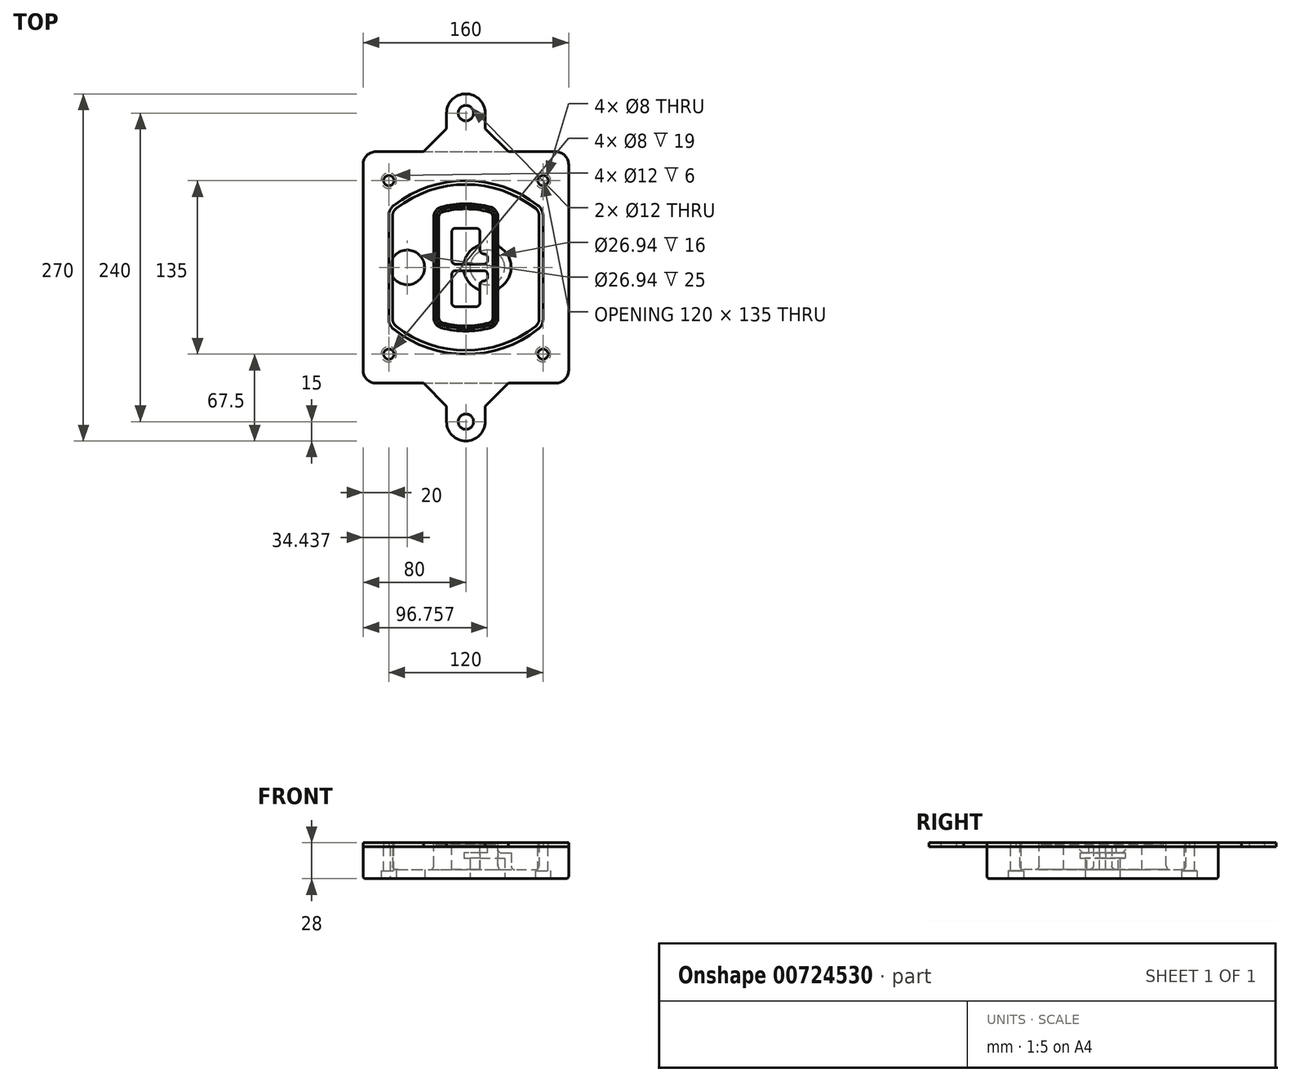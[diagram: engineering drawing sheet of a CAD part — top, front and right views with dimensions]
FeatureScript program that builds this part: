
annotation { "Feature Type Name" : "Feature", "Feature Type Description" : "" }
export const myFeature = defineFeature(function(context is Context, id is Id, definition is map)
    precondition{}
    {
        {
            var Q0;
            Q0=qCreatedBy(makeId("Top.planeOp"),FACE);
            var sketch = newSketch(context, id + "F0", { "sketchPlane" : qUnion([Q0])});
            skPoint(sketch, "E0.rect.middle", {"position": v(0, 0) * mm});
            skLineSegment(sketch, "E1.bottom", {"start": v(-70, -90) * mm, "end": v(70, -90) * mm});
            skLineSegment(sketch, "E1.top", {"start": v(-70, 90) * mm, "end": v(70, 90) * mm});
            skLineSegment(sketch, "E1.left", {"start": v(-80, -80) * mm, "end": v(-80, 80) * mm});
            skLineSegment(sketch, "E1.right", {"start": v(80, -80) * mm, "end": v(80, 80) * mm});
            skLineSegment(sketch, "E2", {"start": v(-80, 90) * mm, "end": v(80, -90) * mm, "construction": true});
            skLineSegment(sketch, "E3", {"start": v(80, 90) * mm, "end": v(-80, -90) * mm, "construction": true});
            skCircle(sketch, "E4", {"center": v(-60, 67.5) * mm, "radius": 4 * mm});
            skCircle(sketch, "E5", {"center": v(60, 67.5) * mm, "radius": 4 * mm});
            skCircle(sketch, "E6", {"center": v(60, -67.5) * mm, "radius": 4 * mm});
            skCircle(sketch, "E7", {"center": v(-60, -67.5) * mm, "radius": 4 * mm});
            skLineSegment(sketch, "E8", {"start": v(-60, 67.5) * mm, "end": v(60, 67.5) * mm, "construction": true});
            skLineSegment(sketch, "E9", {"start": v(60, 67.5) * mm, "end": v(60, -67.5) * mm, "construction": true});
            skLineSegment(sketch, "E10", {"start": v(60, -67.5) * mm, "end": v(-60, -67.5) * mm, "construction": true});
            skLineSegment(sketch, "E11", {"start": v(-60, -67.5) * mm, "end": v(-60, 67.5) * mm, "construction": true});
            skLineSegment(sketch, "E12", {"start": v(-60, 40.3) * mm, "end": v(-60, -40.3) * mm});
            skLineSegment(sketch, "E13", {"start": v(60, 40.3) * mm, "end": v(60, -40.3) * mm});
            skArc(sketch, "E14", {"start": v(56.15, 48.18) * mm, "mid": v(0, 67.5) * mm, "end": v(-56.15, 48.18) * mm});
            skArc(sketch, "E15", {"start": v(-56.15, -48.18) * mm, "mid": v(0, -67.5) * mm, "end": v(56.15, -48.18) * mm});
            skLineSegment(sketch, "E16", {"start": v(-60, 0) * mm, "end": v(60, 0) * mm, "construction": true});
            skPoint(sketch, "E17.visualSharp", {"position": v(-60, -45) * mm});
            skArc(sketch, "E17.filletArc", {"start": v(-60, -40.3) * mm, "mid": v(-58.99, -44.68) * mm, "end": v(-56.15, -48.18) * mm});
            skPoint(sketch, "E18.visualSharp", {"position": v(-60, 45) * mm});
            skArc(sketch, "E18.filletArc", {"start": v(-56.15, 48.18) * mm, "mid": v(-58.99, 44.68) * mm, "end": v(-60, 40.3) * mm});
            skPoint(sketch, "E19.visualSharp", {"position": v(60, 45) * mm});
            skArc(sketch, "E19.filletArc", {"start": v(60, 40.3) * mm, "mid": v(58.99, 44.68) * mm, "end": v(56.15, 48.18) * mm});
            skPoint(sketch, "E20.visualSharp", {"position": v(60, -45) * mm});
            skArc(sketch, "E20.filletArc", {"start": v(56.15, -48.18) * mm, "mid": v(58.99, -44.68) * mm, "end": v(60, -40.3) * mm});
            skPoint(sketch, "E21.visualSharp", {"position": v(-80, 90) * mm});
            skArc(sketch, "E21.filletArc", {"start": v(-70, 90) * mm, "mid": v(-77.07, 87.07) * mm, "end": v(-80, 80) * mm});
            skPoint(sketch, "E22.visualSharp", {"position": v(80, 90) * mm});
            skArc(sketch, "E22.filletArc", {"start": v(80, 80) * mm, "mid": v(77.07, 87.07) * mm, "end": v(70, 90) * mm});
            skPoint(sketch, "E23.visualSharp", {"position": v(80, -90) * mm});
            skArc(sketch, "E23.filletArc", {"start": v(70, -90) * mm, "mid": v(77.07, -87.07) * mm, "end": v(80, -80) * mm});
            skPoint(sketch, "E24.visualSharp", {"position": v(-80, -90) * mm});
            skArc(sketch, "E24.filletArc", {"start": v(-80, -80) * mm, "mid": v(-77.07, -87.07) * mm, "end": v(-70, -90) * mm});
            skArc(sketch, "E25.0", {"start": v(57, 40.3) * mm, "mid": v(56.3, 43.36) * mm, "end": v(54.3, 45.81) * mm});
            skLineSegment(sketch, "E25.1", {"start": v(57, 40.3) * mm, "end": v(57, -40.3) * mm});
            skArc(sketch, "E25.2", {"start": v(54.3, -45.81) * mm, "mid": v(56.3, -43.36) * mm, "end": v(57, -40.3) * mm});
            skArc(sketch, "E25.3", {"start": v(-54.3, -45.81) * mm, "mid": v(0, -64.5) * mm, "end": v(54.3, -45.81) * mm});
            skArc(sketch, "E25.4", {"start": v(-57, -40.3) * mm, "mid": v(-56.3, -43.36) * mm, "end": v(-54.3, -45.81) * mm});
            skArc(sketch, "E25.5", {"start": v(54.3, 45.81) * mm, "mid": v(0, 64.5) * mm, "end": v(-54.3, 45.81) * mm});
            skLineSegment(sketch, "E25.6", {"start": v(-57, 40.3) * mm, "end": v(-57, -40.3) * mm});
            skArc(sketch, "E25.7", {"start": v(-54.3, 45.81) * mm, "mid": v(-56.3, 43.36) * mm, "end": v(-57, 40.3) * mm});
            skArc(sketch, "E26.0", {"start": v(-58.62, 51.33) * mm, "mid": v(-62.58, 46.43) * mm, "end": v(-64, 40.3) * mm});
            skArc(sketch, "E26.1", {"start": v(58.62, 51.33) * mm, "mid": v(0, 71.5) * mm, "end": v(-58.62, 51.33) * mm});
            skArc(sketch, "E26.2", {"start": v(64, 40.3) * mm, "mid": v(62.58, 46.43) * mm, "end": v(58.62, 51.33) * mm});
            skLineSegment(sketch, "E26.3", {"start": v(64, 40.3) * mm, "end": v(64, -40.3) * mm});
            skArc(sketch, "E26.4", {"start": v(58.62, -51.33) * mm, "mid": v(62.58, -46.43) * mm, "end": v(64, -40.3) * mm});
            skLineSegment(sketch, "E26.5", {"start": v(-64, 40.3) * mm, "end": v(-64, -40.3) * mm});
            skArc(sketch, "E26.6", {"start": v(-58.62, -51.33) * mm, "mid": v(0, -71.5) * mm, "end": v(58.62, -51.33) * mm});
            skArc(sketch, "E26.7", {"start": v(-64, -40.3) * mm, "mid": v(-62.58, -46.43) * mm, "end": v(-58.62, -51.33) * mm});
            skSolve(sketch);
        }
        {
            var Q0;
            Q0=makeQuery(id+"F0.imprint","IMPRINT",FACE,{"disambiguationData":[TD([[makeQuery(id+"F0.imprint","IMPRINT",EDGE,{"derivedFrom":sQuery(id+"F0.wireOp",EDGE,"E1.bottom")}),1.0]])]});
            var Q1;
            Q1=makeQuery(id+"F0.imprint","IMPRINT",FACE,{"disambiguationData":[TD([[makeQuery(id+"F0.imprint","IMPRINT",EDGE,{"derivedFrom":sQuery(id+"F0.wireOp",EDGE,"E12")}),1.0]])]});
            var Q2;
            Q2=makeQuery(id+"F0.imprint","IMPRINT",FACE,{"disambiguationData":[TD([[makeQuery(id+"F0.imprint","IMPRINT",EDGE,{"derivedFrom":sQuery(id+"F0.wireOp",EDGE,"E25.0")}),1.0]])]});
            var Q3;
            Q3=makeQuery(id+"F0.imprint","IMPRINT",FACE,{"disambiguationData":[TD([[makeQuery(id+"F0.imprint","IMPRINT",EDGE,{"derivedFrom":sQuery(id+"F0.wireOp",EDGE,"E12")}),-1.0]])]});
            extrude(context, id + "F1", {"entities" : qUnion([Q0, Q1, Q2, Q3]), "oppositeDirection" : true, "depth" : 25 * mm});
        }
        {
            var Q0;
            Q0=makeQuery(id+"F0.imprint","IMPRINT",FACE,{"disambiguationData":[TD([[makeQuery(id+"F0.imprint","IMPRINT",EDGE,{"derivedFrom":sQuery(id+"F0.wireOp",EDGE,"E12")}),1.0]])]});
            extrude(context, id + "F2", {"entities" : qUnion([Q0]), "operationType" : NewBodyOperationType.ADD, "depth" : 3 * mm});
        }
        {
            var Q0;
            Q0=makeQuery(id+"F0.imprint","IMPRINT",FACE,{"disambiguationData":[TD([[makeQuery(id+"F0.imprint","IMPRINT",EDGE,{"derivedFrom":sQuery(id+"F0.wireOp",EDGE,"E25.0")}),1.0]])]});
            extrude(context, id + "F3", {"entities" : qUnion([Q0]), "operationType" : NewBodyOperationType.REMOVE, "oppositeDirection" : true, "depth" : 18 * mm});
        }
        {
            var Q0;
            Q0=makeQuery(id+"F2.opExtrude","CAP_FACE",FACE,{"disambiguationData":[OSD([sQuery(id+"F0.wireOp",EDGE,"E12"),sQuery(id+"F0.wireOp",EDGE,"E13"),sQuery(id+"F0.wireOp",EDGE,"E14"),sQuery(id+"F0.wireOp",EDGE,"E15"),sQuery(id+"F0.wireOp",EDGE,"E17.filletArc"),sQuery(id+"F0.wireOp",EDGE,"E18.filletArc"),sQuery(id+"F0.wireOp",EDGE,"E19.filletArc"),sQuery(id+"F0.wireOp",EDGE,"E20.filletArc"),sQuery(id+"F0.wireOp",EDGE,"E25.0"),sQuery(id+"F0.wireOp",EDGE,"E25.1"),sQuery(id+"F0.wireOp",EDGE,"E25.2"),sQuery(id+"F0.wireOp",EDGE,"E25.3"),sQuery(id+"F0.wireOp",EDGE,"E25.4"),sQuery(id+"F0.wireOp",EDGE,"E25.5"),sQuery(id+"F0.wireOp",EDGE,"E25.6"),sQuery(id+"F0.wireOp",EDGE,"E25.7")])],"isStart":false});
            var sketch = newSketch(context, id + "F4", { "sketchPlane" : qUnion([Q0])});
            skArc(sketch, "E27.0", {"start": v(-19.08, -46.97) * mm, "mid": v(0, -49.5) * mm, "end": v(19.08, -46.97) * mm});
            skArc(sketch, "E28.0", {"start": v(19.08, 46.97) * mm, "mid": v(0, 49.5) * mm, "end": v(-19.08, 46.97) * mm});
            skLineSegment(sketch, "E29", {"start": v(-25, 39.25) * mm, "end": v(-25, -39.25) * mm});
            skLineSegment(sketch, "E30", {"start": v(25, 39.25) * mm, "end": v(25, -39.25) * mm});
            skLineSegment(sketch, "E31", {"start": v(-25, 45.1) * mm, "end": v(25, 45.1) * mm, "construction": true});
            skLineSegment(sketch, "E32", {"start": v(-25, -45.1) * mm, "end": v(25, -45.1) * mm, "construction": true});
            skPoint(sketch, "E33.visualSharp", {"position": v(-25, 45.1) * mm});
            skArc(sketch, "E33.filletArc", {"start": v(-19.08, 46.97) * mm, "mid": v(-23.35, 44.11) * mm, "end": v(-25, 39.25) * mm});
            skPoint(sketch, "E34.visualSharp", {"position": v(25, 45.1) * mm});
            skArc(sketch, "E34.filletArc", {"start": v(25, 39.25) * mm, "mid": v(23.35, 44.11) * mm, "end": v(19.08, 46.97) * mm});
            skPoint(sketch, "E35.visualSharp", {"position": v(25, -45.1) * mm});
            skArc(sketch, "E35.filletArc", {"start": v(19.08, -46.97) * mm, "mid": v(23.35, -44.11) * mm, "end": v(25, -39.25) * mm});
            skPoint(sketch, "E36.visualSharp", {"position": v(-25, -45.1) * mm});
            skArc(sketch, "E36.filletArc", {"start": v(-25, -39.25) * mm, "mid": v(-23.35, -44.11) * mm, "end": v(-19.08, -46.97) * mm});
            skArc(sketch, "E37.0", {"start": v(54.3, 45.81) * mm, "mid": v(0, 64.5) * mm, "end": v(-54.3, 45.81) * mm});
            skArc(sketch, "E37.1", {"start": v(-54.3, 45.81) * mm, "mid": v(-56.3, 43.36) * mm, "end": v(-57, 40.3) * mm});
            skLineSegment(sketch, "E37.2", {"start": v(-57, 40.3) * mm, "end": v(-57, -40.3) * mm});
            skArc(sketch, "E37.3", {"start": v(-57, -40.3) * mm, "mid": v(-56.3, -43.36) * mm, "end": v(-54.3, -45.81) * mm});
            skArc(sketch, "E37.4", {"start": v(-54.3, -45.81) * mm, "mid": v(0, -64.5) * mm, "end": v(54.3, -45.81) * mm});
            skArc(sketch, "E37.5", {"start": v(54.3, -45.81) * mm, "mid": v(56.3, -43.36) * mm, "end": v(57, -40.3) * mm});
            skLineSegment(sketch, "E37.6", {"start": v(57, 40.3) * mm, "end": v(57, -40.3) * mm});
            skArc(sketch, "E37.7", {"start": v(57, 40.3) * mm, "mid": v(56.3, 43.36) * mm, "end": v(54.3, 45.81) * mm});
            skLineSegment(sketch, "E38.0", {"start": v(23, 39.25) * mm, "end": v(23, -39.25) * mm});
            skArc(sketch, "E38.1", {"start": v(18.56, -45.04) * mm, "mid": v(21.76, -42.9) * mm, "end": v(23, -39.25) * mm});
            skArc(sketch, "E38.2", {"start": v(-18.56, -45.04) * mm, "mid": v(0, -47.5) * mm, "end": v(18.56, -45.04) * mm});
            skArc(sketch, "E38.3", {"start": v(-23, -39.25) * mm, "mid": v(-21.76, -42.9) * mm, "end": v(-18.56, -45.04) * mm});
            skLineSegment(sketch, "E38.4", {"start": v(-23, 39.25) * mm, "end": v(-23, -39.25) * mm});
            skArc(sketch, "E38.5", {"start": v(23, 39.25) * mm, "mid": v(21.76, 42.9) * mm, "end": v(18.56, 45.04) * mm});
            skArc(sketch, "E38.6", {"start": v(-18.56, 45.04) * mm, "mid": v(-21.76, 42.9) * mm, "end": v(-23, 39.25) * mm});
            skArc(sketch, "E38.7", {"start": v(18.56, 45.04) * mm, "mid": v(0, 47.5) * mm, "end": v(-18.56, 45.04) * mm});
            skArc(sketch, "E39.0", {"start": v(21, 39.25) * mm, "mid": v(20.18, 41.68) * mm, "end": v(18.04, 43.1) * mm});
            skLineSegment(sketch, "E39.1", {"start": v(21, 39.25) * mm, "end": v(21, -39.25) * mm});
            skArc(sketch, "E39.2", {"start": v(18.04, -43.1) * mm, "mid": v(20.18, -41.68) * mm, "end": v(21, -39.25) * mm});
            skArc(sketch, "E39.3", {"start": v(-18.04, -43.1) * mm, "mid": v(0, -45.5) * mm, "end": v(18.04, -43.1) * mm});
            skArc(sketch, "E39.4", {"start": v(-21, -39.25) * mm, "mid": v(-20.18, -41.68) * mm, "end": v(-18.04, -43.1) * mm});
            skArc(sketch, "E39.5", {"start": v(18.04, 43.1) * mm, "mid": v(0, 45.5) * mm, "end": v(-18.04, 43.1) * mm});
            skLineSegment(sketch, "E39.6", {"start": v(-21, 39.25) * mm, "end": v(-21, -39.25) * mm});
            skArc(sketch, "E39.7", {"start": v(-18.04, 43.1) * mm, "mid": v(-20.18, 41.68) * mm, "end": v(-21, 39.25) * mm});
            skLineSegment(sketch, "E40", {"start": v(-25, 0) * mm, "end": v(25, 0) * mm, "construction": true});
            skLineSegment(sketch, "E41", {"start": v(-11, 5.5) * mm, "end": v(-11, 27.5) * mm});
            skLineSegment(sketch, "E42", {"start": v(-8, 30.5) * mm, "end": v(8, 30.5) * mm});
            skLineSegment(sketch, "E43", {"start": v(11, 27.5) * mm, "end": v(11, 13.5) * mm});
            skLineSegment(sketch, "E44", {"start": v(14, 10.5) * mm, "end": v(14, 10.5) * mm});
            skLineSegment(sketch, "E45", {"start": v(17, 7.5) * mm, "end": v(17, 5.5) * mm});
            skLineSegment(sketch, "E46", {"start": v(14, 2.5) * mm, "end": v(-8, 2.5) * mm});
            skPoint(sketch, "E47.visualSharp", {"position": v(-11, 30.5) * mm});
            skArc(sketch, "E47.filletArc", {"start": v(-8, 30.5) * mm, "mid": v(-10.12, 29.62) * mm, "end": v(-11, 27.5) * mm});
            skPoint(sketch, "E48.visualSharp", {"position": v(11, 30.5) * mm});
            skArc(sketch, "E48.filletArc", {"start": v(11, 27.5) * mm, "mid": v(10.12, 29.62) * mm, "end": v(8, 30.5) * mm});
            skPoint(sketch, "E49.visualSharp", {"position": v(11, 10.5) * mm});
            skArc(sketch, "E49.filletArc", {"start": v(11, 13.5) * mm, "mid": v(11.88, 11.38) * mm, "end": v(14, 10.5) * mm});
            skPoint(sketch, "E50.visualSharp", {"position": v(17, 10.5) * mm});
            skArc(sketch, "E50.filletArc", {"start": v(17, 7.5) * mm, "mid": v(16.12, 9.62) * mm, "end": v(14, 10.5) * mm});
            skPoint(sketch, "E51.visualSharp", {"position": v(17, 2.5) * mm});
            skArc(sketch, "E51.filletArc", {"start": v(14, 2.5) * mm, "mid": v(16.12, 3.38) * mm, "end": v(17, 5.5) * mm});
            skPoint(sketch, "E52.visualSharp", {"position": v(-11, 2.5) * mm});
            skArc(sketch, "E52.filletArc", {"start": v(-11, 5.5) * mm, "mid": v(-10.12, 3.38) * mm, "end": v(-8, 2.5) * mm});
            skLineSegment(sketch, "E53.0.MirrorCS", {"start": v(14, -2.5) * mm, "end": v(-8, -2.5) * mm});
            skArc(sketch, "E54.0.MirrorCS", {"start": v(-11, -5.5) * mm, "mid": v(-10.12, -3.38) * mm, "end": v(-8, -2.5) * mm});
            skLineSegment(sketch, "E55.0.MirrorCS", {"start": v(-11, -5.5) * mm, "end": v(-11, -27.5) * mm});
            skArc(sketch, "E56.0.MirrorCS", {"start": v(-8, -30.5) * mm, "mid": v(-10.12, -29.62) * mm, "end": v(-11, -27.5) * mm});
            skLineSegment(sketch, "E57.0.MirrorCS", {"start": v(-8, -30.5) * mm, "end": v(8, -30.5) * mm});
            skArc(sketch, "E58.0.MirrorCS", {"start": v(11, -27.5) * mm, "mid": v(10.12, -29.62) * mm, "end": v(8, -30.5) * mm});
            skLineSegment(sketch, "E59.0.MirrorCS", {"start": v(11, -27.5) * mm, "end": v(11, -13.5) * mm});
            skArc(sketch, "E60.0.MirrorCS", {"start": v(11, -13.5) * mm, "mid": v(11.88, -11.38) * mm, "end": v(14, -10.5) * mm});
            skArc(sketch, "E61.0.MirrorCS", {"start": v(17, -7.5) * mm, "mid": v(16.12, -9.62) * mm, "end": v(14, -10.5) * mm});
            skLineSegment(sketch, "E62.0.MirrorCS", {"start": v(17, -7.5) * mm, "end": v(17, -5.5) * mm});
            skArc(sketch, "E63.0.MirrorCS", {"start": v(14, -2.5) * mm, "mid": v(16.12, -3.38) * mm, "end": v(17, -5.5) * mm});
            skSolve(sketch);
        }
        {
            var Q0;
            Q0=makeQuery(id+"F4.imprint","IMPRINT",FACE,{"disambiguationData":[TD([[makeQuery(id+"F4.imprint","IMPRINT",EDGE,{"derivedFrom":sQuery(id+"F4.wireOp",EDGE,"E27.0")}),1.0]])]});
            var Q1;
            Q1=makeQuery(id+"F4.imprint","IMPRINT",FACE,{"disambiguationData":[TD([[makeQuery(id+"F4.imprint","IMPRINT",EDGE,{"derivedFrom":sQuery(id+"F4.wireOp",EDGE,"E38.0")}),-1.0]])]});
            var Q2;
            Q2=makeQuery(id+"F4.imprint","IMPRINT",FACE,{"disambiguationData":[TD([[makeQuery(id+"F4.imprint","IMPRINT",EDGE,{"derivedFrom":sQuery(id+"F4.wireOp",EDGE,"E39.0")}),1.0]])]});
            extrude(context, id + "F5", {"entities" : qUnion([Q0, Q1, Q2]), "operationType" : NewBodyOperationType.ADD, "endBound" : BoundingType.UP_TO_NEXT, "oppositeDirection" : true, "depth" : 25 * mm});
        }
        {
            var Q0;
            Q0=makeQuery(id+"F4.imprint","IMPRINT",FACE,{"disambiguationData":[TD([[makeQuery(id+"F4.imprint","IMPRINT",EDGE,{"derivedFrom":sQuery(id+"F4.wireOp",EDGE,"E38.0")}),-1.0]])]});
            extrude(context, id + "F6", {"entities" : qUnion([Q0]), "operationType" : NewBodyOperationType.REMOVE, "oppositeDirection" : true, "depth" : 2 * mm});
        }
        {
            var Q0;
            Q0=makeQuery(id+"F1.opExtrude","CAP_FACE",FACE,{"disambiguationData":[OSD([sQuery(id+"F0.wireOp",EDGE,"E1.bottom"),sQuery(id+"F0.wireOp",EDGE,"E1.top"),sQuery(id+"F0.wireOp",EDGE,"E1.left"),sQuery(id+"F0.wireOp",EDGE,"E1.right"),sQuery(id+"F0.wireOp",EDGE,"E4"),sQuery(id+"F0.wireOp",EDGE,"E5"),sQuery(id+"F0.wireOp",EDGE,"E6"),sQuery(id+"F0.wireOp",EDGE,"E7"),sQuery(id+"F0.wireOp",EDGE,"E21.filletArc"),sQuery(id+"F0.wireOp",EDGE,"E22.filletArc"),sQuery(id+"F0.wireOp",EDGE,"E23.filletArc"),sQuery(id+"F0.wireOp",EDGE,"E24.filletArc")])],"isStart":false});
            var sketch = newSketch(context, id + "F7", { "sketchPlane" : qUnion([Q0])});
            skCircle(sketch, "E64", {"center": v(16.76, 0) * mm, "radius": 13.47 * mm});
            skCircle(sketch, "E65", {"center": v(-45.56, 0) * mm, "radius": 13.47 * mm});
            skLineSegment(sketch, "E66", {"start": v(80, 0) * mm, "end": v(-80, 0) * mm});
            skCircle(sketch, "E67", {"center": v(16.76, 0) * mm, "radius": 18.47 * mm});
            skCircle(sketch, "E68", {"center": v(60, -67.5) * mm, "radius": 6 * mm});
            skCircle(sketch, "E69", {"center": v(-60, -67.5) * mm, "radius": 6 * mm});
            skCircle(sketch, "E70", {"center": v(-60, 67.5) * mm, "radius": 6 * mm});
            skCircle(sketch, "E71", {"center": v(60, 67.5) * mm, "radius": 6 * mm});
            skSolve(sketch);
        }
        {
            var Q0;
            {var subQ1=sQuery(id+"F7.wireOp",EDGE,"E66");var subQ4=sQuery(id+"F7.wireOp",EDGE,"E64");var subQ6=makeQuery(id+"F7.imprint","INTERSECT",VERTEX,{"disambiguationData":[OD(0.0)],"derivedFrom":[subQ4,subQ1]});Q0=makeQuery(id+"F7.imprint","IMPRINT",FACE,{"disambiguationData":[TD([[makeQuery(id+"F7.imprint","IMPRINT",EDGE,{"disambiguationData":[TD([[subQ6,-1.0]])],"derivedFrom":subQ4}),-1.0]])]});}
            var Q1;
            {var subQ0=sQuery(id+"F7.wireOp",EDGE,"E66");var subQ1=sQuery(id+"F7.wireOp",EDGE,"E64");var subQ3=makeQuery(id+"F7.imprint","INTERSECT",VERTEX,{"disambiguationData":[OD(0.0)],"derivedFrom":[subQ1,subQ0]});Q1=makeQuery(id+"F7.imprint","IMPRINT",FACE,{"disambiguationData":[TD([[makeQuery(id+"F7.imprint","IMPRINT",EDGE,{"disambiguationData":[TD([[subQ3,-1.0]])],"derivedFrom":subQ1}),1.0]])]});}
            var Q2;
            {var subQ0=sQuery(id+"F7.wireOp",EDGE,"E66");var subQ1=sQuery(id+"F7.wireOp",EDGE,"E64");var subQ3=makeQuery(id+"F7.imprint","INTERSECT",VERTEX,{"disambiguationData":[OD(0.0)],"derivedFrom":[subQ1,subQ0]});Q2=makeQuery(id+"F7.imprint","IMPRINT",FACE,{"disambiguationData":[TD([[makeQuery(id+"F7.imprint","IMPRINT",EDGE,{"disambiguationData":[TD([[subQ3,1.0]])],"derivedFrom":subQ1}),1.0]])]});}
            var Q3;
            {var subQ1=sQuery(id+"F7.wireOp",EDGE,"E66");var subQ4=sQuery(id+"F7.wireOp",EDGE,"E64");var subQ6=makeQuery(id+"F7.imprint","INTERSECT",VERTEX,{"disambiguationData":[OD(0.0)],"derivedFrom":[subQ4,subQ1]});Q3=makeQuery(id+"F7.imprint","IMPRINT",FACE,{"disambiguationData":[TD([[makeQuery(id+"F7.imprint","IMPRINT",EDGE,{"disambiguationData":[TD([[subQ6,1.0]])],"derivedFrom":subQ4}),-1.0]])]});}
            extrude(context, id + "F8", {"entities" : qUnion([Q0, Q1, Q2, Q3]), "operationType" : NewBodyOperationType.ADD, "oppositeDirection" : true, "depth" : 20 * mm});
        }
        {
            var Q0;
            {var subQ0=sQuery(id+"F7.wireOp",EDGE,"E66");var subQ1=sQuery(id+"F7.wireOp",EDGE,"E64");var subQ3=makeQuery(id+"F7.imprint","INTERSECT",VERTEX,{"disambiguationData":[OD(0.0)],"derivedFrom":[subQ1,subQ0]});Q0=makeQuery(id+"F7.imprint","IMPRINT",FACE,{"disambiguationData":[TD([[makeQuery(id+"F7.imprint","IMPRINT",EDGE,{"disambiguationData":[TD([[subQ3,-1.0]])],"derivedFrom":subQ1}),1.0]])]});}
            var Q1;
            {var subQ0=sQuery(id+"F7.wireOp",EDGE,"E66");var subQ1=sQuery(id+"F7.wireOp",EDGE,"E64");var subQ3=makeQuery(id+"F7.imprint","INTERSECT",VERTEX,{"disambiguationData":[OD(0.0)],"derivedFrom":[subQ1,subQ0]});Q1=makeQuery(id+"F7.imprint","IMPRINT",FACE,{"disambiguationData":[TD([[makeQuery(id+"F7.imprint","IMPRINT",EDGE,{"disambiguationData":[TD([[subQ3,1.0]])],"derivedFrom":subQ1}),1.0]])]});}
            extrude(context, id + "F9", {"entities" : qUnion([Q0, Q1]), "operationType" : NewBodyOperationType.REMOVE, "oppositeDirection" : true, "depth" : 16 * mm});
        }
        {
            var Q0;
            {var subQ0=sQuery(id+"F7.wireOp",EDGE,"E66");var subQ1=sQuery(id+"F7.wireOp",EDGE,"E65");var subQ3=makeQuery(id+"F7.imprint","INTERSECT",VERTEX,{"disambiguationData":[OD(0.0)],"derivedFrom":[subQ1,subQ0]});Q0=makeQuery(id+"F7.imprint","IMPRINT",FACE,{"disambiguationData":[TD([[makeQuery(id+"F7.imprint","IMPRINT",EDGE,{"disambiguationData":[TD([[subQ3,-1.0]])],"derivedFrom":subQ1}),1.0]])]});}
            var Q1;
            {var subQ0=sQuery(id+"F7.wireOp",EDGE,"E66");var subQ1=sQuery(id+"F7.wireOp",EDGE,"E65");var subQ3=makeQuery(id+"F7.imprint","INTERSECT",VERTEX,{"disambiguationData":[OD(0.0)],"derivedFrom":[subQ1,subQ0]});Q1=makeQuery(id+"F7.imprint","IMPRINT",FACE,{"disambiguationData":[TD([[makeQuery(id+"F7.imprint","IMPRINT",EDGE,{"disambiguationData":[TD([[subQ3,1.0]])],"derivedFrom":subQ1}),1.0]])]});}
            extrude(context, id + "F10", {"entities" : qUnion([Q0, Q1]), "operationType" : NewBodyOperationType.REMOVE, "oppositeDirection" : true, "depth" : 25 * mm});
        }
        {
            var Q0;
            Q0=makeQuery(id+"F7.imprint","IMPRINT",FACE,{"disambiguationData":[TD([[makeQuery(id+"F7.imprint","IMPRINT",EDGE,{"derivedFrom":sQuery(id+"F7.wireOp",EDGE,"E68")}),1.0]])]});
            var Q1;
            Q1=makeQuery(id+"F7.imprint","IMPRINT",FACE,{"disambiguationData":[TD([[makeQuery(id+"F7.imprint","IMPRINT",EDGE,{"derivedFrom":makeQuery(id+"F1.opExtrude","CAP_EDGE",EDGE,{"disambiguationData":[OSD([sQuery(id+"F0.wireOp",EDGE,"E5")])],"isStart":false})}),-1.0]])]});
            var Q2;
            Q2=makeQuery(id+"F7.imprint","IMPRINT",FACE,{"disambiguationData":[TD([[makeQuery(id+"F7.imprint","IMPRINT",EDGE,{"derivedFrom":sQuery(id+"F7.wireOp",EDGE,"E69")}),1.0]])]});
            var Q3;
            Q3=makeQuery(id+"F7.imprint","IMPRINT",FACE,{"disambiguationData":[TD([[makeQuery(id+"F7.imprint","IMPRINT",EDGE,{"derivedFrom":makeQuery(id+"F1.opExtrude","CAP_EDGE",EDGE,{"disambiguationData":[OSD([sQuery(id+"F0.wireOp",EDGE,"E4")])],"isStart":false})}),-1.0]])]});
            var Q4;
            Q4=makeQuery(id+"F7.imprint","IMPRINT",FACE,{"disambiguationData":[TD([[makeQuery(id+"F7.imprint","IMPRINT",EDGE,{"derivedFrom":sQuery(id+"F7.wireOp",EDGE,"E70")}),1.0]])]});
            var Q5;
            Q5=makeQuery(id+"F7.imprint","IMPRINT",FACE,{"disambiguationData":[TD([[makeQuery(id+"F7.imprint","IMPRINT",EDGE,{"derivedFrom":makeQuery(id+"F1.opExtrude","CAP_EDGE",EDGE,{"disambiguationData":[OSD([sQuery(id+"F0.wireOp",EDGE,"E7")])],"isStart":false})}),-1.0]])]});
            var Q6;
            Q6=makeQuery(id+"F7.imprint","IMPRINT",FACE,{"disambiguationData":[TD([[makeQuery(id+"F7.imprint","IMPRINT",EDGE,{"derivedFrom":sQuery(id+"F7.wireOp",EDGE,"E71")}),1.0]])]});
            var Q7;
            Q7=makeQuery(id+"F7.imprint","IMPRINT",FACE,{"disambiguationData":[TD([[makeQuery(id+"F7.imprint","IMPRINT",EDGE,{"derivedFrom":makeQuery(id+"F1.opExtrude","CAP_EDGE",EDGE,{"disambiguationData":[OSD([sQuery(id+"F0.wireOp",EDGE,"E6")])],"isStart":false})}),-1.0]])]});
            extrude(context, id + "F11", {"entities" : qUnion([Q0, Q1, Q2, Q3, Q4, Q5, Q6, Q7]), "operationType" : NewBodyOperationType.REMOVE, "oppositeDirection" : true, "depth" : 6 * mm});
        }
        {
            var Q0;
            Q0=makeQuery(id+"F9.boolean.opBoolean","COPY",FACE,{"derivedFrom":makeQuery(id+"F9.opExtrude","CAP_FACE",FACE,{"disambiguationData":[OSD([sQuery(id+"F7.wireOp",EDGE,"E64")])],"isStart":false})});
            var sketch = newSketch(context, id + "F12", { "sketchPlane" : qUnion([Q0])});
            skArc(sketch, "E72.0", {"start": v(11, 17.55) * mm, "mid": v(2.57, 11.82) * mm, "end": v(-1.54, 2.5) * mm});
            skArc(sketch, "E72.1", {"start": v(-1.54, -2.5) * mm, "mid": v(2.57, -11.82) * mm, "end": v(11, -17.55) * mm});
            skLineSegment(sketch, "E73", {"start": v(-1.54, -2.5) * mm, "end": v(14, -2.5) * mm});
            skLineSegment(sketch, "E74.0", {"start": v(14, 2.5) * mm, "end": v(-1.54, 2.5) * mm});
            skArc(sketch, "E74.1", {"start": v(14, 2.5) * mm, "mid": v(16.12, 3.38) * mm, "end": v(17, 5.5) * mm});
            skLineSegment(sketch, "E74.2", {"start": v(17, 7.5) * mm, "end": v(17, 5.5) * mm});
            skArc(sketch, "E74.3", {"start": v(17, 7.5) * mm, "mid": v(16.12, 9.62) * mm, "end": v(14, 10.5) * mm});
            skArc(sketch, "E74.4", {"start": v(11, 13.5) * mm, "mid": v(11.88, 11.38) * mm, "end": v(14, 10.5) * mm});
            skLineSegment(sketch, "E74.5", {"start": v(11, 17.55) * mm, "end": v(11, 13.5) * mm});
            skLineSegment(sketch, "E74.7", {"start": v(14, -2.5) * mm, "end": v(-1.54, -2.5) * mm});
            skArc(sketch, "E74.8", {"start": v(14, -2.5) * mm, "mid": v(16.12, -3.38) * mm, "end": v(17, -5.5) * mm});
            skLineSegment(sketch, "E74.9", {"start": v(17, -7.5) * mm, "end": v(17, -5.5) * mm});
            skArc(sketch, "E74.10", {"start": v(17, -7.5) * mm, "mid": v(16.12, -9.62) * mm, "end": v(14, -10.5) * mm});
            skArc(sketch, "E74.11", {"start": v(11, -13.5) * mm, "mid": v(11.88, -11.38) * mm, "end": v(14, -10.5) * mm});
            skLineSegment(sketch, "E74.12", {"start": v(11, -17.55) * mm, "end": v(11, -13.5) * mm});
            skPoint(sketch, "E75.orphan", {"position": v(11, -27.5) * mm});
            skPoint(sketch, "E76.orphan", {"position": v(-8, -2.5) * mm});
            skPoint(sketch, "E77.orphan", {"position": v(-8, 2.5) * mm});
            skPoint(sketch, "E78.orphan", {"position": v(11, 27.5) * mm});
            skSolve(sketch);
        }
        {
            var Q0;
            {var subQ7=sQuery(id+"F12.wireOp",EDGE,"E72.0");var subQ14=sQuery(id+"F12.wireOp",EDGE,"E72.1");var subQ16=sQuery(id+"F12.wireOp",EDGE,"E74.1");var subQ18=sQuery(id+"F12.wireOp",EDGE,"E74.8");Q0=qUnion([makeQuery(id+"F12.imprint","IMPRINT",FACE,{"disambiguationData":[TD([[makeQuery(id+"F12.imprint","IMPRINT",EDGE,{"derivedFrom":subQ7}),1.0]])]}),makeQuery(id+"F12.imprint","IMPRINT",FACE,{"disambiguationData":[TD([[makeQuery(id+"F12.imprint","IMPRINT",EDGE,{"derivedFrom":subQ14}),1.0]])]}),makeQuery(id+"F12.imprint","IMPRINT",FACE,{"disambiguationData":[TD([[makeQuery(id+"F12.imprint","IMPRINT",EDGE,{"derivedFrom":subQ16}),1.0]])]}),makeQuery(id+"F12.imprint","IMPRINT",FACE,{"disambiguationData":[TD([[makeQuery(id+"F12.imprint","IMPRINT",EDGE,{"derivedFrom":subQ18}),-1.0]])]})]);}
            var Q1;
            Q1=makeQuery(id+"F5.boolean.opBoolean","SPLIT",FACE,{"disambiguationData":[TD([makeQuery(id+"F5.opExtrude","SWEPT_FACE",FACE,{"disambiguationData":[OSD([sQuery(id+"F4.wireOp",EDGE,"E41")])]})])],"derivedFrom":makeQuery(id+"F3.boolean.opBoolean","COPY",FACE,{"derivedFrom":makeQuery(id+"F3.opExtrude","CAP_FACE",FACE,{"disambiguationData":[OSD([sQuery(id+"F0.wireOp",EDGE,"E25.0"),sQuery(id+"F0.wireOp",EDGE,"E25.1"),sQuery(id+"F0.wireOp",EDGE,"E25.2"),sQuery(id+"F0.wireOp",EDGE,"E25.3"),sQuery(id+"F0.wireOp",EDGE,"E25.4"),sQuery(id+"F0.wireOp",EDGE,"E25.5"),sQuery(id+"F0.wireOp",EDGE,"E25.6"),sQuery(id+"F0.wireOp",EDGE,"E25.7")])],"isStart":false})})});
            extrude(context, id + "F13", {"entities" : qUnion([Q0]), "operationType" : NewBodyOperationType.REMOVE, "endBound" : BoundingType.UP_TO_SURFACE, "endBoundEntityFace" : qUnion([Q1]), "depth" : 25 * mm});
        }
        {
            var Q0;
            Q0=makeQuery(id+"F3.boolean.opBoolean","COPY",EDGE,{"derivedFrom":makeQuery(id+"F3.opExtrude","CAP_EDGE",EDGE,{"disambiguationData":[OSD([sQuery(id+"F0.wireOp",EDGE,"E25.6")])],"isStart":false})});
            var Q1;
            Q1=makeQuery(id+"F8.boolean.opBoolean","INTERSECT",EDGE,{"derivedFrom":[makeQuery(id+"F5.opExtrude","SWEPT_FACE",FACE,{"disambiguationData":[OSD([sQuery(id+"F4.wireOp",EDGE,"E30")])]}),makeQuery(id+"F8.opExtrude","CAP_FACE",FACE,{"disambiguationData":[OSD([sQuery(id+"F7.wireOp",EDGE,"E67")])],"isStart":false})]});
            var Q2;
            Q2=makeQuery(id+"F8.boolean.opBoolean","INTERSECT",EDGE,{"disambiguationData":[OD(1.0)],"derivedFrom":[makeQuery(id+"F5.opExtrude","SWEPT_FACE",FACE,{"disambiguationData":[OSD([sQuery(id+"F4.wireOp",EDGE,"E30")])]}),makeQuery(id+"F8.opExtrude","SWEPT_FACE",FACE,{"disambiguationData":[OSD([sQuery(id+"F7.wireOp",EDGE,"E67")])]})]});
            var Q3;
            {var subQ0=sQuery(id+"F4.wireOp",EDGE,"E30");Q3=makeQuery(id+"F8.boolean.opBoolean","SPLIT",EDGE,{"disambiguationData":[TD([makeQuery(id+"F5.opExtrude","SWEPT_FACE",FACE,{"disambiguationData":[OSD([sQuery(id+"F4.wireOp",EDGE,"E35.filletArc")])]})])],"derivedFrom":makeQuery(id+"F5.opExtrude","CAP_EDGE",EDGE,{"disambiguationData":[OSD([subQ0])],"isStart":false})});}
            var Q4;
            {var subQ0=sQuery(id+"F0.wireOp",EDGE,"E25.7");var subQ1=sQuery(id+"F0.wireOp",EDGE,"E25.1");var subQ2=sQuery(id+"F0.wireOp",EDGE,"E25.6");var subQ3=sQuery(id+"F0.wireOp",EDGE,"E25.5");var subQ4=sQuery(id+"F0.wireOp",EDGE,"E25.4");var subQ5=sQuery(id+"F0.wireOp",EDGE,"E25.0");var subQ6=sQuery(id+"F0.wireOp",EDGE,"E25.2");var subQ7=sQuery(id+"F0.wireOp",EDGE,"E25.3");Q4=makeQuery(id+"F8.boolean.opBoolean","INTERSECT",EDGE,{"derivedFrom":[makeQuery(id+"F5.boolean.opBoolean","SPLIT",FACE,{"disambiguationData":[TD([makeQuery(id+"F2.opExtrude","SWEPT_FACE",FACE,{"disambiguationData":[OSD([subQ5])]})])],"derivedFrom":makeQuery(id+"F3.boolean.opBoolean","COPY",FACE,{"derivedFrom":makeQuery(id+"F3.opExtrude","CAP_FACE",FACE,{"disambiguationData":[OSD([subQ5,subQ1,subQ6,subQ7,subQ4,subQ3,subQ2,subQ0])],"isStart":false})})}),makeQuery(id+"F8.opExtrude","SWEPT_FACE",FACE,{"disambiguationData":[OSD([sQuery(id+"F7.wireOp",EDGE,"E67")])]})]});}
            var Q5;
            Q5=makeQuery(id+"F8.boolean.opBoolean","INTERSECT",EDGE,{"disambiguationData":[OD(0.0)],"derivedFrom":[makeQuery(id+"F5.opExtrude","SWEPT_FACE",FACE,{"disambiguationData":[OSD([sQuery(id+"F4.wireOp",EDGE,"E30")])]}),makeQuery(id+"F8.opExtrude","SWEPT_FACE",FACE,{"disambiguationData":[OSD([sQuery(id+"F7.wireOp",EDGE,"E67")])]})]});
            fillet(context, id + "F14", {"entities" : qUnion([Q0, Q1, Q2, Q3, Q4, Q5]), "radius" : 3 * mm, "tangentPropagation" : true, "allowEdgeOverflow" : false});
        }
        {
            var Q0;
            Q0=makeQuery(id+"F1.opExtrude","CAP_EDGE",EDGE,{"disambiguationData":[OSD([sQuery(id+"F0.wireOp",EDGE,"E1.bottom")])],"isStart":false});
            fillet(context, id + "F15", {"entities" : qUnion([Q0]), "radius" : 2 * mm, "tangentPropagation" : true, "allowEdgeOverflow" : false});
        }
        {
            var Q0;
            {var subQ0=sQuery(id+"F0.wireOp",EDGE,"E21.filletArc");var subQ1=sQuery(id+"F0.wireOp",EDGE,"E7");var subQ2=sQuery(id+"F0.wireOp",EDGE,"E6");var subQ3=sQuery(id+"F0.wireOp",EDGE,"E5");var subQ4=sQuery(id+"F0.wireOp",EDGE,"E4");var subQ5=sQuery(id+"F0.wireOp",EDGE,"E22.filletArc");var subQ6=sQuery(id+"F0.wireOp",EDGE,"E1.bottom");var subQ7=sQuery(id+"F0.wireOp",EDGE,"E1.right");var subQ8=sQuery(id+"F0.wireOp",EDGE,"E1.top");var subQ9=sQuery(id+"F0.wireOp",EDGE,"E1.left");var subQ10=sQuery(id+"F0.wireOp",EDGE,"E23.filletArc");var subQ11=sQuery(id+"F0.wireOp",EDGE,"E24.filletArc");Q0=makeQuery(id+"F2.boolean.opBoolean","SPLIT",FACE,{"disambiguationData":[TD([makeQuery(id+"F1.opExtrude","SWEPT_FACE",FACE,{"disambiguationData":[OSD([subQ6])]})])],"derivedFrom":makeQuery(id+"F1.opExtrude","CAP_FACE",FACE,{"disambiguationData":[OSD([subQ6,subQ8,subQ9,subQ7,subQ4,subQ3,subQ2,subQ1,subQ0,subQ5,subQ10,subQ11])],"isStart":true})});}
            var sketch = newSketch(context, id + "F16", { "sketchPlane" : qUnion([Q0])});
            skLineSegment(sketch, "E79.0", {"start": v(-70, 90) * mm, "end": v(70, 90) * mm});
            skArc(sketch, "E79.1", {"start": v(-70, 90) * mm, "mid": v(-77.07, 87.07) * mm, "end": v(-80, 80) * mm});
            skLineSegment(sketch, "E79.2", {"start": v(-80, -80) * mm, "end": v(-80, 80) * mm});
            skArc(sketch, "E79.3", {"start": v(-80, -80) * mm, "mid": v(-77.07, -87.07) * mm, "end": v(-70, -90) * mm});
            skLineSegment(sketch, "E79.4", {"start": v(-70, -90) * mm, "end": v(70, -90) * mm});
            skArc(sketch, "E79.5", {"start": v(70, -90) * mm, "mid": v(77.07, -87.07) * mm, "end": v(80, -80) * mm});
            skLineSegment(sketch, "E79.6", {"start": v(80, -80) * mm, "end": v(80, 80) * mm});
            skArc(sketch, "E79.7", {"start": v(80, 80) * mm, "mid": v(77.07, 87.07) * mm, "end": v(70, 90) * mm});
            skCircle(sketch, "E79.8", {"center": v(-60, 67.5) * mm, "radius": 4 * mm});
            skCircle(sketch, "E79.9", {"center": v(60, 67.5) * mm, "radius": 4 * mm});
            skCircle(sketch, "E79.10", {"center": v(60, -67.5) * mm, "radius": 4 * mm});
            skCircle(sketch, "E79.11", {"center": v(-60, -67.5) * mm, "radius": 4 * mm});
            skLineSegment(sketch, "E80", {"start": v(-80, 0) * mm, "end": v(80, 0) * mm, "construction": true});
            skLineSegment(sketch, "E81", {"start": v(0, 90) * mm, "end": v(0, 120) * mm, "construction": true});
            skLineSegment(sketch, "E82", {"start": v(-33, 90) * mm, "end": v(-15, 108) * mm});
            skLineSegment(sketch, "E83", {"start": v(33, 90) * mm, "end": v(15, 108) * mm});
            skCircle(sketch, "E84", {"center": v(0, 120) * mm, "radius": 6 * mm});
            skArc(sketch, "E85", {"start": v(-15, 120) * mm, "mid": v(0, 135) * mm, "end": v(15, 120) * mm});
            skLineSegment(sketch, "E86", {"start": v(-15, 108) * mm, "end": v(-15, 120) * mm});
            skLineSegment(sketch, "E87", {"start": v(15, 108) * mm, "end": v(15, 120) * mm});
            skLineSegment(sketch, "E88.MirrorCS", {"start": v(-15, -108) * mm, "end": v(-15, -120) * mm});
            skLineSegment(sketch, "E89.MirrorCS", {"start": v(-33, -90) * mm, "end": v(-15, -108) * mm});
            skLineSegment(sketch, "E90.MirrorCS", {"start": v(33, -90) * mm, "end": v(15, -108) * mm});
            skLineSegment(sketch, "E91.MirrorCS", {"start": v(15, -108) * mm, "end": v(15, -120) * mm});
            skArc(sketch, "E92.MirrorCS", {"start": v(-15, -120) * mm, "mid": v(0, -135) * mm, "end": v(15, -120) * mm});
            skCircle(sketch, "E93.MirrorC", {"center": v(0, -120) * mm, "radius": 6 * mm});
            skSolve(sketch);
        }
        {
            var Q0;
            Q0=makeQuery(id+"F16.imprint","IMPRINT",FACE,{"disambiguationData":[TD([[makeQuery(id+"F16.imprint","IMPRINT",EDGE,{"derivedFrom":sQuery(id+"F16.wireOp",EDGE,"LAyB9Eon-A8TJ-eU6J-R6AS-ih3Y1rFErONo")}),-1.0]])]});
            var Q1;
            {var subQ1=sQuery(id+"F16.wireOp",EDGE,"E79.1");Q1=makeQuery(id+"F16.imprint","IMPRINT",FACE,{"disambiguationData":[TD([[makeQuery(id+"F16.imprint","IMPRINT",EDGE,{"derivedFrom":subQ1}),1.0]])]});}
            var Q2;
            Q2=makeQuery(id+"F16.imprint","IMPRINT",FACE,{"disambiguationData":[TD([[makeQuery(id+"F16.imprint","IMPRINT",EDGE,{"derivedFrom":sQuery(id+"F16.wireOp",EDGE,"LAyB9Eon-A8TJ-eU6J-R6AS-ih3Y1rFErONo")}),1.0]])]});
            var Q3;
            {var subQ1=sQuery(id+"F16.wireOp",EDGE,"7e09a80c-e641-4784-bf9e-b96955cbc9d70.MirrorCS");Q3=makeQuery(id+"F16.imprint","IMPRINT",FACE,{"disambiguationData":[TD([[makeQuery(id+"F16.imprint","IMPRINT",EDGE,{"derivedFrom":subQ1}),1.0]])]});}
            var Q4;
            {var subQ1=sQuery(id+"F16.wireOp",EDGE,"E82");Q4=makeQuery(id+"F16.imprint","IMPRINT",FACE,{"disambiguationData":[TD([[makeQuery(id+"F16.imprint","IMPRINT",EDGE,{"derivedFrom":subQ1}),-1.0]])]});}
            var Q5;
            {var subQ1=sQuery(id+"F16.wireOp",EDGE,"E89.MirrorCS");Q5=makeQuery(id+"F16.imprint","IMPRINT",FACE,{"disambiguationData":[TD([[makeQuery(id+"F16.imprint","IMPRINT",EDGE,{"derivedFrom":subQ1}),1.0]])]});}
            var Q6;
            Q6=makeQuery(id+"F2.opExtrude","CAP_FACE",FACE,{"disambiguationData":[OSD([sQuery(id+"F0.wireOp",EDGE,"E12"),sQuery(id+"F0.wireOp",EDGE,"E13"),sQuery(id+"F0.wireOp",EDGE,"E14"),sQuery(id+"F0.wireOp",EDGE,"E15"),sQuery(id+"F0.wireOp",EDGE,"E17.filletArc"),sQuery(id+"F0.wireOp",EDGE,"E18.filletArc"),sQuery(id+"F0.wireOp",EDGE,"E19.filletArc"),sQuery(id+"F0.wireOp",EDGE,"E20.filletArc"),sQuery(id+"F0.wireOp",EDGE,"E25.0"),sQuery(id+"F0.wireOp",EDGE,"E25.1"),sQuery(id+"F0.wireOp",EDGE,"E25.2"),sQuery(id+"F0.wireOp",EDGE,"E25.3"),sQuery(id+"F0.wireOp",EDGE,"E25.4"),sQuery(id+"F0.wireOp",EDGE,"E25.5"),sQuery(id+"F0.wireOp",EDGE,"E25.6"),sQuery(id+"F0.wireOp",EDGE,"E25.7")])],"isStart":false});
            extrude(context, id + "F17", {"entities" : qUnion([Q0, Q1, Q2, Q3, Q4, Q5]), "endBound" : BoundingType.UP_TO_SURFACE, "endBoundEntityFace" : qUnion([Q6]), "depth" : 25 * mm});
        }
    });
